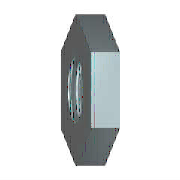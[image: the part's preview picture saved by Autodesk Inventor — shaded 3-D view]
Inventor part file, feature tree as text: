
AUTODESK INVENTOR PART (.ipt)
format: ipt  version: 2020 (Build 240168000, 168)  size: 130,048 bytes
history: native  units: mm (DEFAULTED — no unit token found)
features: hole x1, other x1, plane x1, sketch x1
ambient origin geometry x7: Origin, YZ Plane, XZ Plane, X Axis, Y Axis, Z Axis, Center Point
bodies: Solid1 (feature_tree), Body (feature_tree)
feature tree (4):
  hole  "Thread"  [1 undecoded]
  other  "Work Axis1"
  plane  "Work Plane1"
  sketch  "Sketch1"  dims[d0=8.082904mm d1=2.2mm d2=0.0mm d3=3.242mm d4=6.0mm d5=4.0mm d6=2.0mm d7=14.3117mm d8=8.0mm d9=20.594885mm d10=0.378886mm d11=30.0deg d12=0.378886mm d13=30.0deg d15=0.0mm d17=0.0mm d18=0.378886mm d19=0.378886mm d20=0.0mm d21=0.0mm]
note: 1 required parameter value undecoded (feature->parameter linkage not recoverable at this tier; creation-order binding heuristic only, values carry confidence <= 0.55)
